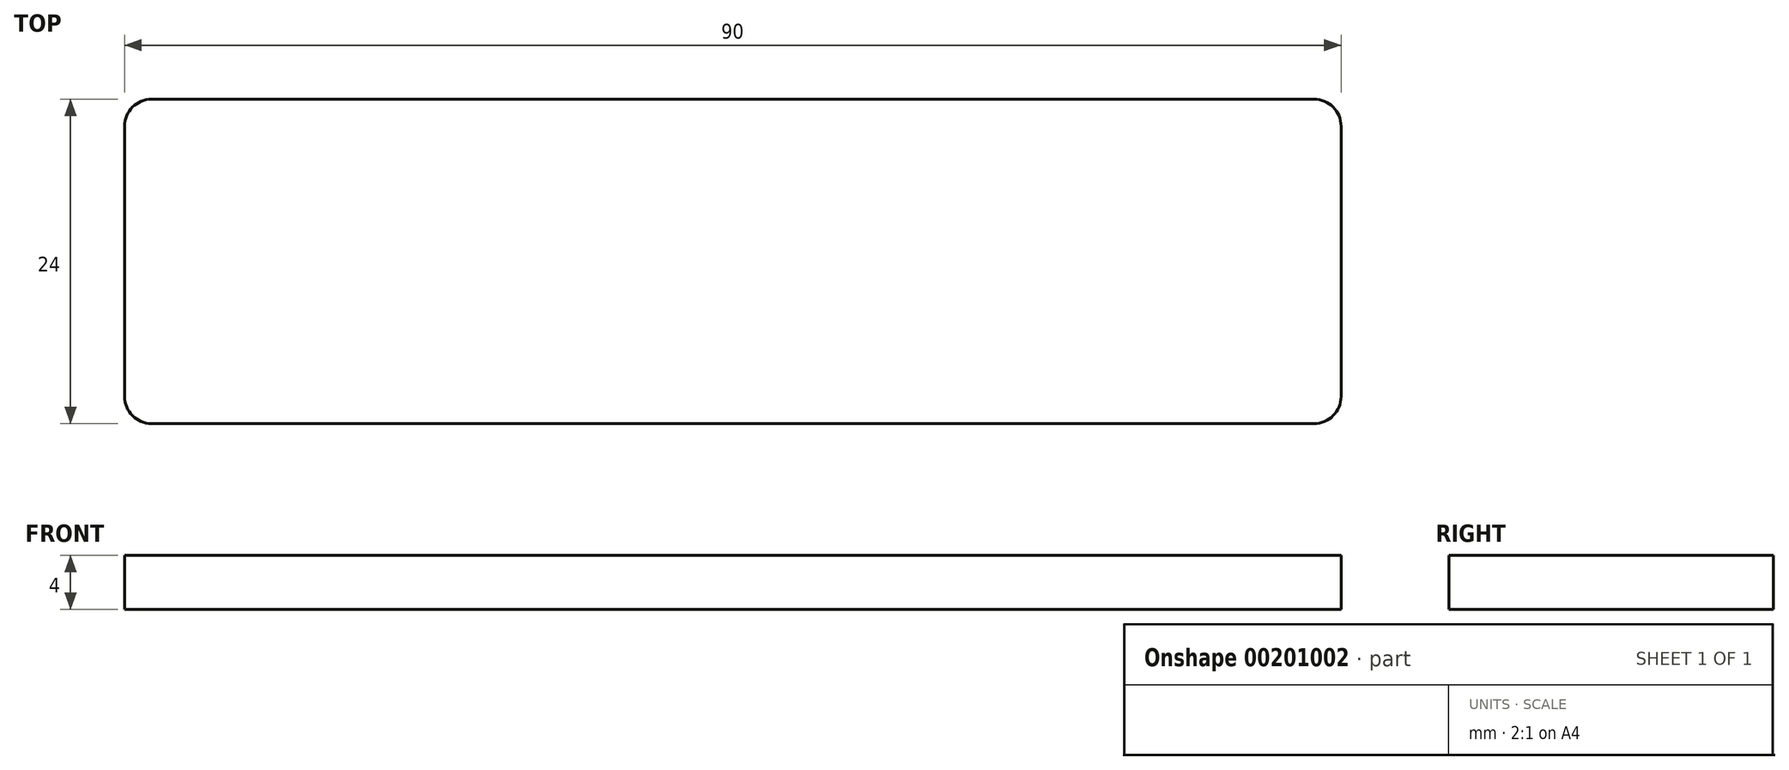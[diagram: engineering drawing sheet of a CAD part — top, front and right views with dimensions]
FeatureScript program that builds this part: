
annotation { "Feature Type Name" : "Feature", "Feature Type Description" : "" }
export const myFeature = defineFeature(function(context is Context, id is Id, definition is map)
    precondition{}
    {
        {
            var Q0;
            Q0=qCreatedBy(makeId("Top.planeOp"),FACE);
            var sketch = newSketch(context, id + "F0", { "sketchPlane" : qUnion([Q0])});
            skLineSegment(sketch, "E0.bottom", {"start": v(-45, 12) * mm, "end": v(45, 12) * mm});
            skLineSegment(sketch, "E0.top", {"start": v(-45, -12) * mm, "end": v(45, -12) * mm});
            skLineSegment(sketch, "E0.left", {"start": v(-45, 12) * mm, "end": v(-45, -12) * mm});
            skLineSegment(sketch, "E0.right", {"start": v(45, 12) * mm, "end": v(45, -12) * mm});
            skLineSegment(sketch, "E1", {"start": v(0, -12) * mm, "end": v(0, 12) * mm, "construction": true});
            skSolve(sketch);
        }
        {
            var Q0;
            Q0=makeQuery(id+"F0.imprint","IMPRINT",FACE,{"disambiguationData":[TD([[makeQuery(id+"F0.imprint","IMPRINT",EDGE,{"derivedFrom":sQuery(id+"F0.wireOp",EDGE,"E0.bottom")}),-1.0]])]});
            extrude(context, id + "F1", {"entities" : qUnion([Q0]), "depth" : 4 * mm});
        }
        {
            var Q0;
            Q0=makeQuery(id+"F1.opExtrude","SWEPT_EDGE",EDGE,{"disambiguationData":[OSD([sQuery(id+"F0.wireOp",EDGE,"E0.top"),sQuery(id+"F0.wireOp",EDGE,"E0.left")])]});
            var Q1;
            Q1=makeQuery(id+"F1.opExtrude","SWEPT_EDGE",EDGE,{"disambiguationData":[OSD([sQuery(id+"F0.wireOp",EDGE,"E0.bottom"),sQuery(id+"F0.wireOp",EDGE,"E0.right")])]});
            var Q2;
            Q2=makeQuery(id+"F1.opExtrude","SWEPT_EDGE",EDGE,{"disambiguationData":[OSD([sQuery(id+"F0.wireOp",EDGE,"E0.bottom"),sQuery(id+"F0.wireOp",EDGE,"E0.left")])]});
            var Q3;
            Q3=makeQuery(id+"F1.opExtrude","SWEPT_EDGE",EDGE,{"disambiguationData":[OSD([sQuery(id+"F0.wireOp",EDGE,"E0.top"),sQuery(id+"F0.wireOp",EDGE,"E0.right")])]});
            fillet(context, id + "F2", {"entities" : qUnion([Q0, Q1, Q2, Q3]), "radius" : 2 * mm, "tangentPropagation" : true, "allowEdgeOverflow" : false});
        }
    });
